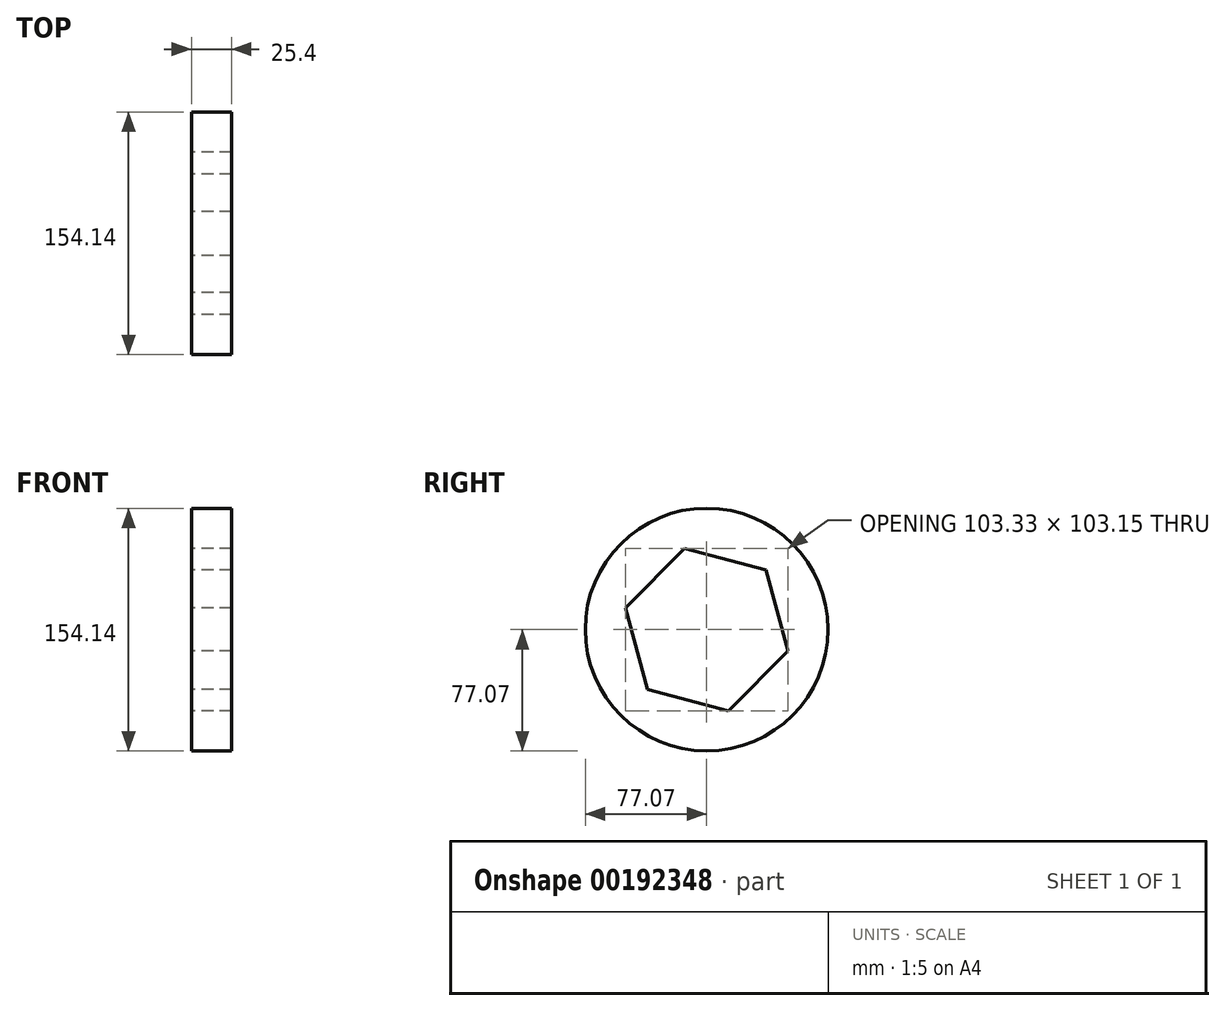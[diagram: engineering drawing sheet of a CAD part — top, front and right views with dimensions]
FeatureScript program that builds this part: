
annotation { "Feature Type Name" : "Feature", "Feature Type Description" : "" }
export const myFeature = defineFeature(function(context is Context, id is Id, definition is map)
    precondition{}
    {
        {
            var Q0;
            Q0=qCreatedBy(makeId("Right.planeOp"),FACE);
            var sketch = newSketch(context, id + "F0", { "sketchPlane" : qUnion([Q0])});
            skCircle(sketch, "E0", {"center": v(0, 0) * mm, "radius": 77.07 * mm});
            skSolve(sketch);
        }
        {
            var Q0;
            Q0 = qSketchRegion(id + "F0", true);
            extrude(context, id + "F1", {"entities" : qUnion([Q0]), "depth" : 25.4 * mm});
        }
        {
            var Q0;
            Q0=makeQuery(id+"F1.opExtrude","CAP_FACE",FACE,{"disambiguationData":[OSD([sQuery(id+"F0.wireOp",EDGE,"E0")])],"isStart":true});
            var sketch = newSketch(context, id + "F2", { "sketchPlane" : qUnion([Q0])});
            skCircle(sketch, "E1.cCircle", {"center": v(0, 0) * mm, "radius": 46.28 * mm, "construction": true});
            skLineSegment(sketch, "E1.0", {"start": v(14, 51.58) * mm, "end": v(51.66, 13.67) * mm});
            skLineSegment(sketch, "E1.1", {"start": v(51.66, 13.67) * mm, "end": v(37.67, -37.9) * mm});
            skLineSegment(sketch, "E1.2", {"start": v(37.67, -37.9) * mm, "end": v(-14, -51.58) * mm});
            skLineSegment(sketch, "E1.3", {"start": v(-14, -51.58) * mm, "end": v(-51.66, -13.67) * mm});
            skLineSegment(sketch, "E1.4", {"start": v(-51.66, -13.67) * mm, "end": v(-37.67, 37.9) * mm});
            skLineSegment(sketch, "E1.5", {"start": v(-37.67, 37.9) * mm, "end": v(14, 51.58) * mm});
            skPoint(sketch, "E1.0.midPoint", {"position": v(32.83, 32.62) * mm});
            skSolve(sketch);
        }
        {
            var Q0;
            Q0=makeQuery(id+"F2.imprint","IMPRINT",FACE,{"disambiguationData":[TD([[makeQuery(id+"F2.imprint","IMPRINT",EDGE,{"derivedFrom":sQuery(id+"F2.wireOp",EDGE,"E1.0")}),-1.0]])]});
            extrude(context, id + "F3", {"entities" : qUnion([Q0]), "operationType" : NewBodyOperationType.REMOVE, "oppositeDirection" : true, "depth" : 25.4 * mm});
        }
    });
